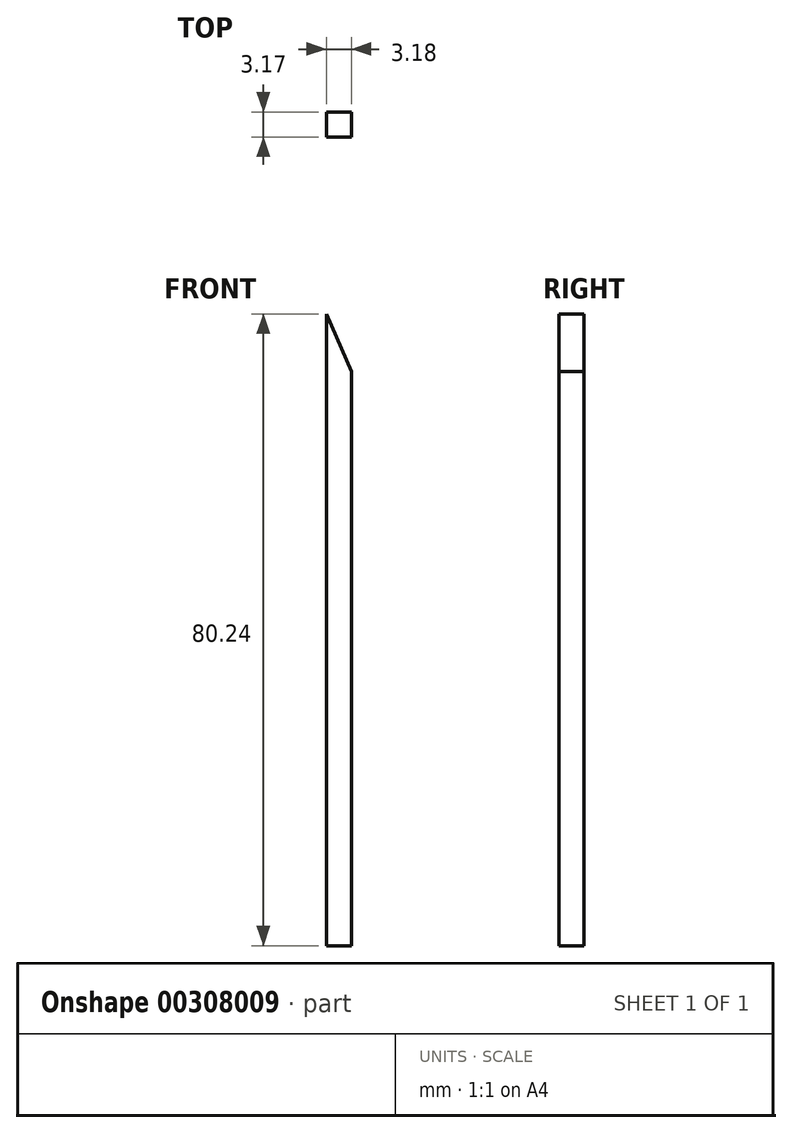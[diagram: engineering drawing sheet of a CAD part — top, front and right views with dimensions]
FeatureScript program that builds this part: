
annotation { "Feature Type Name" : "Feature", "Feature Type Description" : "" }
export const myFeature = defineFeature(function(context is Context, id is Id, definition is map)
    precondition{}
    {
        {
            var Q0;
            Q0=qCreatedBy(makeId("Front.planeOp"),FACE);
            var sketch = newSketch(context, id + "F0", { "sketchPlane" : qUnion([Q0])});
            skLineSegment(sketch, "E0", {"start": v(0, 0) * mm, "end": v(3.18, 0) * mm});
            skLineSegment(sketch, "E1", {"start": v(3.18, 0) * mm, "end": v(3.18, 72.94) * mm});
            skLineSegment(sketch, "E2", {"start": v(3.18, 72.94) * mm, "end": v(0, 80.24) * mm});
            skLineSegment(sketch, "E3", {"start": v(0, 80.24) * mm, "end": v(0, 0) * mm});
            skSolve(sketch);
        }
        {
            var Q0;
            Q0=makeQuery(id+"F0.imprint","IMPRINT",FACE,{"disambiguationData":[TD([[makeQuery(id+"F0.imprint","IMPRINT",EDGE,{"derivedFrom":sQuery(id+"F0.wireOp",EDGE,"E0")}),1.0]])]});
            extrude(context, id + "F1", {"entities" : qUnion([Q0]), "depth" : 3.17 * mm});
        }
    });
